# Revit family: LOROWERK 00630-100X
name_source: partatom
category: Pipe Fittings
revit_build: Autodesk Revit 2017 (Build: 20160225_1515(x64)
units: mm (PartAtom-declared; Revit-internal decimal feet)

## family parameters
Always vertical = Yes
Cut with Voids When Loaded = No
Part Type = Union
Round Connector Dimension = Use Diameter
Shared = No
Work Plane-Based = No

## types (1)
- LOROWERK 00630-100X
    BIM = https://media.stage.bim.site
    Benennung = LORO-X Anschlussstück an SML+KA-Muffe 100, DN100
    Bestellmenge (Multiplikator) = 1
    Brandschutzklasse = B1 nach DIN 4102
    CONNECTOR0_DIAMETER_dZ_0r = 100 mm  [stored 0.328084 ft]
    CONNECTOR0_dZ_00 = 106 mm
    CONNECTOR0_dZ_01 = 180 mm
    CONNECTOR0_ref_dZ = 106 mm
    CONNECTOR1_DIAMETER_dZ_0r = 100 mm  [stored 0.328084 ft]
    CONNECTOR1_dZ_01 = 74 mm
    CONNECTOR1_ref_dZ = 74 mm
    DATANORM = 00630.100X
    Description = LORO-X Stahlabflussrohre
    Formstück-Gewicht [kg] = 1
    GTIN = 4038088027806
    HAN = 00630.100X
    HeinzeBIM = https://www.heinze.de
    Index = 20
    Index Number = 6
    LOROWERK 00630.100X en Visibility = Yes
    Manufacturer = LOROWERK K.H. Vahlbrauk GmbH & Co. KG
    Nenndruck = 0.5
    Nenndrucksystem = PN
    Nennweitensystem = DN
    Normen/Regeln/Zulassungen = DVGW für Trinkwasser
    Produktbezeichnung = Entsorgung
    Produktbezeichnung Text = LORO-X Stahlabflussrohre
    Produktkennung = Formstück
    Produktname = Anschlussstücke von LORO-X Rohr an Kunststoffabflussrohrmuffen (KA)
    Produktvideo = https://media.stage.bim.site
    Querschnittsform = rund
    Type Name = Anschlussstücke von LORO-X Rohr an Kunststoffabflussrohrmuffen (KA)
    VDIBSN = 020001???001001???00100100000100300700000000000170000000000000000006
    Verbindungsart I = Pressen
    Verbindungsart II = axial pressen
    Verlegeart = Unterputz
    max. zul. Dauer-Betriebstemperatur [°C] = 95

note: [stored X ft] marks values corroborated as IEEE doubles in the binary element streams (Revit-internal decimal feet)

## geometry (parser evidence)
native form markers: Blend x2
no freeform markers — native parametric forms only
